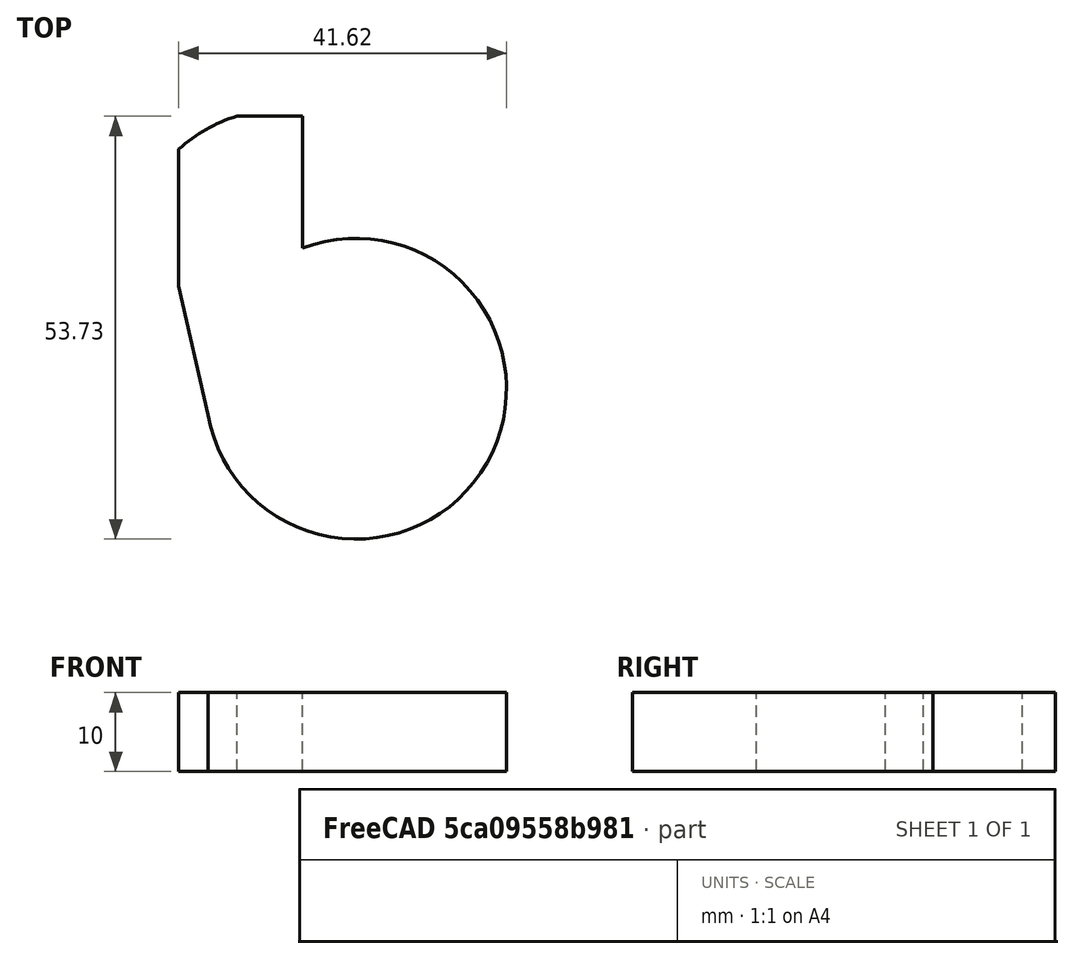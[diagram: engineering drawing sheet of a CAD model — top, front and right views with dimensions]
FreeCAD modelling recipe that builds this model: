
FCSTD DOCUMENT  (FreeCAD 0.17R13541 (Git))
Label: EmpreinteGrenouille_V190205-1621
License: All rights reserved
LicenseURL: http://en.wikipedia.org/wiki/All_rights_reserved
objects: Sketcher::SketchObject×4, PartDesign::Body×3, PartDesign::Pad×1
note: 9 computed .brp shape members not serialized (recipe doc carries the construction recipe); baked Part::Feature solids carry a one-line shape summary decoded from their .brp

FEATURE [Sketcher::SketchObject] Sketch
  MapMode = 5
  Support = -> [XY_Plane]
  sketch-geometry (7):
    g0: ArcOfCircle CenterX=0.0946023 CenterY=0 CenterZ=0 NormalX=0 NormalY=0 NormalZ=1 AngleXU=0 Radius=19.1 StartAngle=3.31082 EndAngle=8.21517
    g1: LineSegment StartX=-6.655 StartY=17.8676 StartZ=0 EndX=-6.655 EndY=34.8536 EndZ=0
    g2: LineSegment StartX=-6.655 StartY=34.8536 StartZ=0 EndX=-15.1403 EndY=34.8536 EndZ=0
    g3: LineSegment StartX=-22.655 StartY=30.5082 StartZ=0 EndX=-22.655 EndY=13.3416 EndZ=0
    g4: LineSegment StartX=-6.655 StartY=17.8676 StartZ=0 EndX=-6.655 EndY=34.8536 EndZ=0
    g5: LineSegment StartX=-22.655 StartY=13.3416 StartZ=0 EndX=-18.7326 EndY=-3.21675 EndZ=0
    g6: ArcOfCircle CenterX=-9.52931 CenterY=16.4796 CenterZ=0 NormalX=0 NormalY=0 NormalZ=1 AngleXU=0 Radius=19.2116 StartAngle=1.86718 EndAngle=2.32296
  constraints (13):
    c: Radius(g0) = 19.1
    c: Vertical(g1)
    c: Coincident(g4,g2)
    c: Horizontal(g2)
    c: Vertical(g3)
    c: Vertical(g4)
    c: Coincident(g2,g1)
    c: Coincident(g5,g3)
    c: Coincident(g0,g5)
    c: Coincident(g1,g0)
    c: PointOnObject(g4,g0)
    c: Coincident(g6,g2)
    c: Coincident(g6,g3)
FEATURE [PartDesign::Body] Body
  Group = -> [Sketch]
  Origin = -> Origin
FEATURE [Sketcher::SketchObject] Sketch001
  MapMode = 5
  Support = -> [XY_Plane001]
  sketch-geometry (17):
    g0: Circle CenterX=0.0946023 CenterY=0 CenterZ=0 NormalX=0 NormalY=0 NormalZ=1 AngleXU=0 Radius=19.1
    g1: LineSegment StartX=6.655 StartY=-2.94644 StartZ=0 EndX=-6.655 EndY=-2.94644 EndZ=0
    g2: LineSegment StartX=-6.655 StartY=-2.94644 StartZ=0 EndX=-6.655 EndY=34.8536 EndZ=0
    g3: LineSegment StartX=-6.655 StartY=34.8536 StartZ=0 EndX=6.655 EndY=34.8536 EndZ=0
    g4: LineSegment StartX=6.655 StartY=34.8536 StartZ=0 EndX=6.655 EndY=-2.94644 EndZ=0
    g5: LineSegment StartX=-6.655 StartY=34.8536 StartZ=0 EndX=-22.655 EndY=34.8536 EndZ=0
    g6: LineSegment StartX=-22.655 StartY=34.8536 StartZ=0 EndX=-22.655 EndY=13.3416 EndZ=0
    g7: LineSegment StartX=-22.655 StartY=13.3416 StartZ=0 EndX=-6.655 EndY=13.3416 EndZ=0
    g8: LineSegment StartX=-6.655 StartY=13.3416 StartZ=0 EndX=-6.655 EndY=34.8536 EndZ=0
    g9: LineSegment StartX=6.70355 StartY=34.8398 StartZ=0 EndX=22.7035 EndY=34.8398 EndZ=0
    g10: LineSegment StartX=22.7035 StartY=34.8398 StartZ=0 EndX=22.7035 EndY=11.8651 EndZ=0
    g11: LineSegment StartX=22.7035 StartY=11.8651 StartZ=0 EndX=6.70355 EndY=11.8651 EndZ=0
    g12: LineSegment StartX=6.70355 StartY=11.8651 StartZ=0 EndX=6.70355 EndY=34.8398 EndZ=0
    g13: Circle CenterX=0 CenterY=0 CenterZ=0 NormalX=0 NormalY=0 NormalZ=1 AngleXU=0 Radius=38
    g14: LineSegment StartX=-22.655 StartY=13.3416 StartZ=0 EndX=-18.7326 EndY=-3.21675 EndZ=0
    g15: LineSegment StartX=-18.7326 StartY=-3.21675 StartZ=0 EndX=18.9218 EndY=-3.21675 EndZ=0
    g16: LineSegment StartX=18.9218 StartY=-3.21675 StartZ=0 EndX=22.7035 EndY=11.8651 EndZ=0
  constraints (40):
    c: Radius(g0) = 19.1
    c: Coincident(g1,g2)
    c: Coincident(g2,g3)
    c: Coincident(g3,g4)
    c: Coincident(g4,g1)
    c: Horizontal(g1)
    c: Horizontal(g3)
    c: Vertical(g2)
    c: Vertical(g4)
    c: Distance(g-1,g4) = 6.655
    c: Distance(g1) = 13.31
    c: Distance(g4) = 37.8
    c: Coincident(g5,g6)
    c: Coincident(g6,g7)
    c: Coincident(g7,g8)
    c: Coincident(g8,g5)
    c: Horizontal(g5)
    c: Horizontal(g7)
    c: Vertical(g6)
    c: Vertical(g8)
    c: Coincident(g5,g2)
    c: Distance(g7) = 16
    c: Coincident(g9,g10)
    c: Coincident(g10,g11)
    c: Coincident(g11,g12)
    c: Coincident(g12,g9)
    c: Horizontal(g9)
    c: Horizontal(g11)
    c: Vertical(g10)
    c: Vertical(g12)
    c: Distance(g11) = 16
    c: Radius(g13) = 38
    c: Coincident(g13,g-1)
    c: Coincident(g14,g6)
    c: PointOnObject(g14,g0)
    c: Coincident(g15,g14)
    c: PointOnObject(g15,g0)
    c: Horizontal(g15)
    c: Coincident(g16,g15)
    c: Coincident(g16,g10)
FEATURE [PartDesign::Body] Body001
  Group = -> [Sketch001]
  Origin = -> Origin001
FEATURE [Sketcher::SketchObject] Sketch002
  MapMode = 5
  Support = -> [XY_Plane002]
  sketch-geometry (6):
    g0: ArcOfCircle CenterX=0 CenterY=0 CenterZ=0 NormalX=0 NormalY=0 NormalZ=1 AngleXU=0 Radius=19.1 StartAngle=3.31612 EndAngle=8.21778
    g1: LineSegment StartX=-6.79637 StartY=34.6286 StartZ=0 EndX=-6.79637 EndY=17.8499 EndZ=0
    g2: LineSegment StartX=-6.79637 StartY=34.6286 StartZ=0 EndX=-15.1159 EndY=34.6286 EndZ=0
    g3: LineSegment StartX=-22.5226 StartY=30.4255 StartZ=0 EndX=-22.5226 EndY=13.0518 EndZ=0
    g4: LineSegment StartX=-22.5226 StartY=13.0518 StartZ=0 EndX=-18.8098 EndY=-3.31657 EndZ=0
    g5: ArcOfCircle CenterX=-9.66454 CenterY=16.3948 CenterZ=0 NormalX=0 NormalY=0 NormalZ=1 AngleXU=0 Radius=19.0313 StartAngle=1.86131 EndAngle=2.31261
  constraints (12):
    c: Coincident(g-1,g0)
    c: Radius(g0) = 19.1
    c: Vertical(g1)
    c: Coincident(g2,g1)
    c: Horizontal(g2)
    c: Vertical(g3)
    c: PointOnObject(g-1,g5)
    c: Coincident(g5,g2)
    c: Coincident(g5,g3)
    c: Coincident(g0,g1)
    c: Coincident(g0,g4)
    c: Coincident(g3,g4)
FEATURE [Sketcher::SketchObject] Sketch003
  MapMode = 5
  Support = -> [XY_Plane]
  sketch-geometry (7):
    g0: ArcOfCircle CenterX=0.0946023 CenterY=0 CenterZ=0 NormalX=0 NormalY=0 NormalZ=1 AngleXU=0 Radius=19.1 StartAngle=3.31082 EndAngle=8.21517
    g1: LineSegment StartX=-6.655 StartY=17.8676 StartZ=0 EndX=-6.655 EndY=34.8536 EndZ=0
    g2: LineSegment StartX=-6.655 StartY=34.8536 StartZ=0 EndX=-15.1403 EndY=34.8536 EndZ=0
    g3: LineSegment StartX=-22.655 StartY=30.5082 StartZ=0 EndX=-22.655 EndY=13.3416 EndZ=0
    g4: LineSegment StartX=-6.655 StartY=17.8676 StartZ=0 EndX=-6.655 EndY=34.8536 EndZ=0
    g5: LineSegment StartX=-22.655 StartY=13.3416 StartZ=0 EndX=-18.7326 EndY=-3.21675 EndZ=0
    g6: ArcOfCircle CenterX=-9.52931 CenterY=16.4796 CenterZ=0 NormalX=0 NormalY=0 NormalZ=1 AngleXU=0 Radius=19.2116 StartAngle=1.86718 EndAngle=2.32296
  constraints (13):
    c: Radius(g0) = 19.1
    c: Vertical(g1)
    c: Coincident(g4,g2)
    c: Horizontal(g2)
    c: Vertical(g3)
    c: Vertical(g4)
    c: Coincident(g2,g1)
    c: Coincident(g5,g3)
    c: Coincident(g0,g5)
    c: Coincident(g1,g0)
    c: PointOnObject(g4,g0)
    c: Coincident(g6,g2)
    c: Coincident(g6,g3)
FEATURE [PartDesign::Pad] Pad
  Length = 10
  Length2 = 100
  Profile = -> Sketch002
  Type = 0
FEATURE [PartDesign::Body] Body002
  Group = -> [Sketch002,Pad]
  Origin = -> Origin002
  Tip = -> Pad
